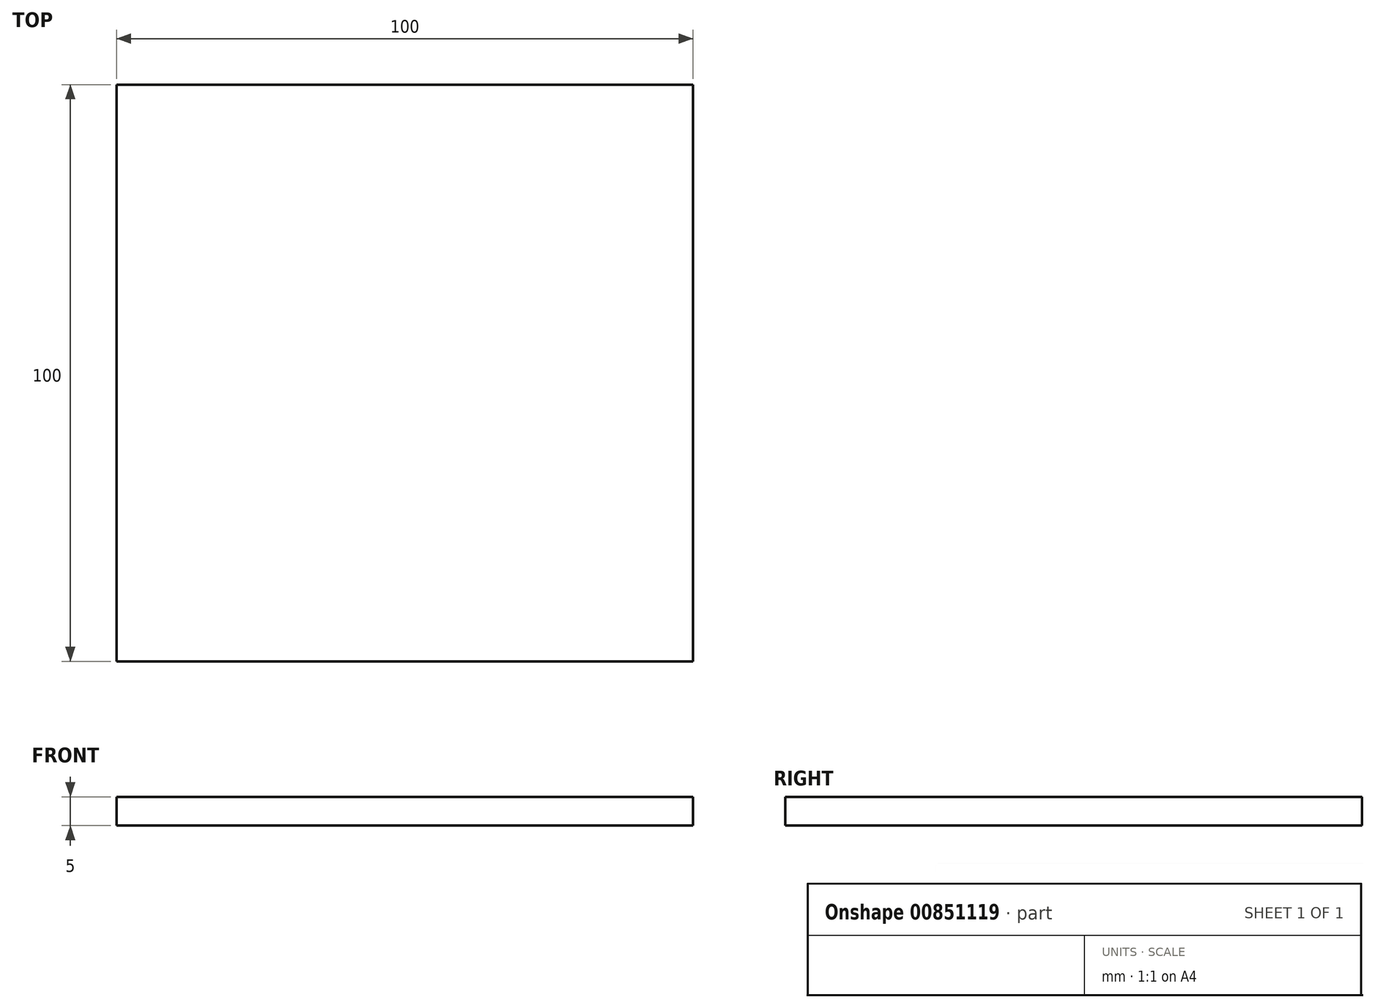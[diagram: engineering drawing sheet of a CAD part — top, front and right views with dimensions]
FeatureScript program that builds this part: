
annotation { "Feature Type Name" : "Feature", "Feature Type Description" : "" }
export const myFeature = defineFeature(function(context is Context, id is Id, definition is map)
    precondition{}
    {
        {
            var Q0;
            Q0=qCreatedBy(makeId("Top.planeOp"),FACE);
            var sketch = newSketch(context, id + "F0", { "sketchPlane" : qUnion([Q0])});
            skLineSegment(sketch, "E0.bottom", {"start": v(50, -50) * mm, "end": v(-50, -50) * mm});
            skLineSegment(sketch, "E0.top", {"start": v(50, 50) * mm, "end": v(-50, 50) * mm});
            skLineSegment(sketch, "E0.left", {"start": v(50, -50) * mm, "end": v(50, 50) * mm});
            skLineSegment(sketch, "E0.right", {"start": v(-50, -50) * mm, "end": v(-50, 50) * mm});
            skPoint(sketch, "E0.middle", {"position": v(0, 0) * mm});
            skSolve(sketch);
        }
        {
            var Q0;
            Q0=makeQuery(id+"F0.imprint","IMPRINT",FACE,{"disambiguationData":[TD([[makeQuery(id+"F0.imprint","IMPRINT",EDGE,{"derivedFrom":sQuery(id+"F0.wireOp",EDGE,"E0.bottom")}),-1.0]])]});
            extrude(context, id + "F1", {"entities" : qUnion([Q0]), "depth" : 5 * mm, "offsetDistance" : 25 * mm});
        }
    });
